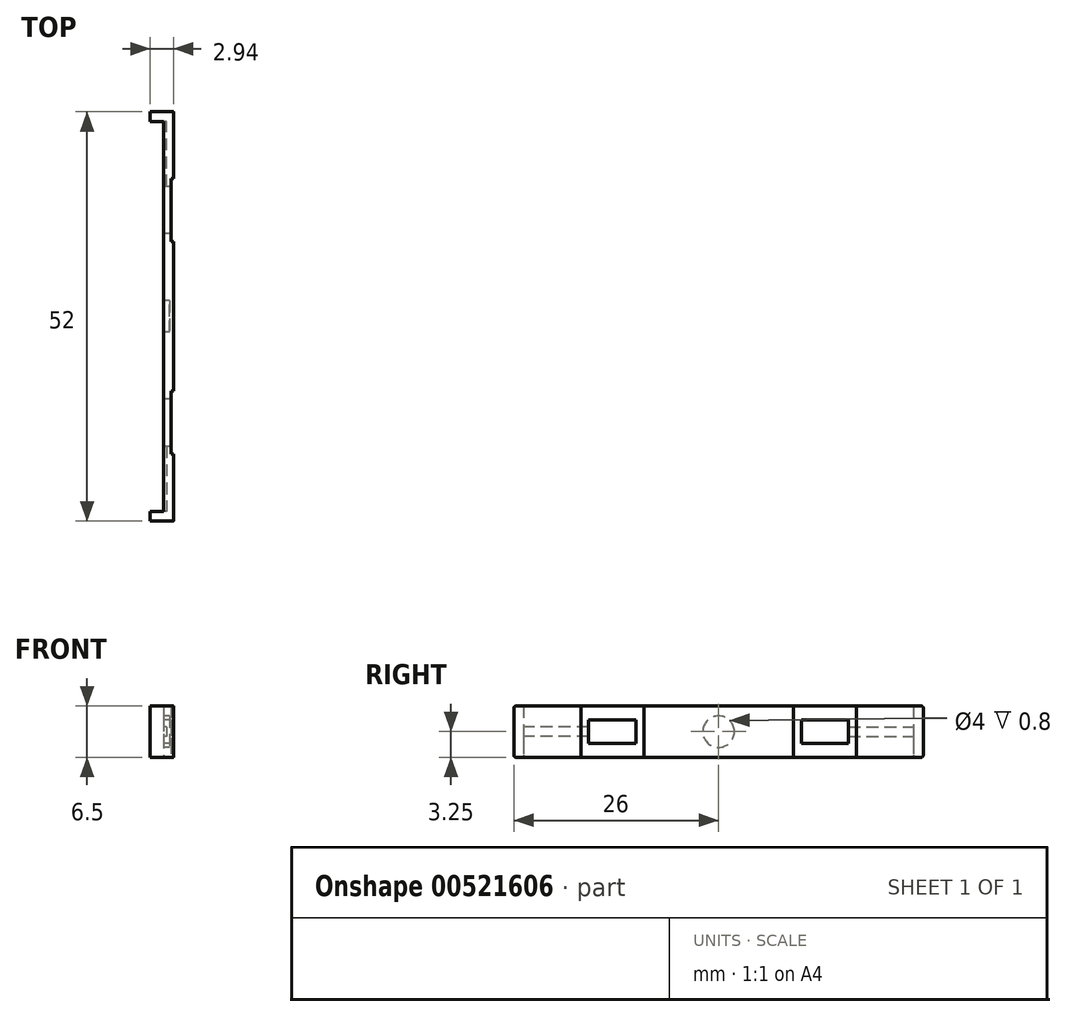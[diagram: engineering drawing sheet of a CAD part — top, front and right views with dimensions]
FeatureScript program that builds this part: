
annotation { "Feature Type Name" : "Feature", "Feature Type Description" : "" }
export const myFeature = defineFeature(function(context is Context, id is Id, definition is map)
    precondition{}
    {
        {
            var Q0;
            Q0=qCreatedBy(makeId("Right.planeOp"),FACE);
            var sketch = newSketch(context, id + "F0", { "sketchPlane" : qUnion([Q0])});
            skLineSegment(sketch, "E0.bottom", {"start": v(26, 3.25) * mm, "end": v(-26, 3.25) * mm});
            skLineSegment(sketch, "E0.top", {"start": v(26, -3.25) * mm, "end": v(-26, -3.25) * mm});
            skLineSegment(sketch, "E0.left", {"start": v(26, 3.25) * mm, "end": v(26, -3.25) * mm});
            skLineSegment(sketch, "E0.right", {"start": v(-26, 3.25) * mm, "end": v(-26, -3.25) * mm});
            skPoint(sketch, "E0.middle", {"position": v(0, 0) * mm});
            skSolve(sketch);
        }
        {
            var Q0;
            Q0=makeQuery(id+"F0.imprint","IMPRINT",FACE,{"disambiguationData":[TD([[makeQuery(id+"F0.imprint","IMPRINT",EDGE,{"derivedFrom":sQuery(id+"F0.wireOp",EDGE,"E0.bottom")}),1.0]])]});
            extrude(context, id + "F1", {"entities" : qUnion([Q0]), "endBound" : BoundingType.SYMMETRIC, "depth" : 1.25 * mm, "offsetDistance" : 25 * mm});
        }
        {
            var Q0;
            Q0=makeQuery(id+"F1.opExtrude","CAP_FACE",FACE,{"disambiguationData":[OSD([sQuery(id+"F0.wireOp",EDGE,"E0.bottom"),sQuery(id+"F0.wireOp",EDGE,"E0.top"),sQuery(id+"F0.wireOp",EDGE,"E0.left"),sQuery(id+"F0.wireOp",EDGE,"E0.right")])],"isStart":true});
            var sketch = newSketch(context, id + "F2", { "sketchPlane" : qUnion([Q0])});
            skLineSegment(sketch, "E1.bottom", {"start": v(-26, 3.25) * mm, "end": v(-24.75, 3.25) * mm});
            skLineSegment(sketch, "E1.top", {"start": v(-26, -3.25) * mm, "end": v(-24.75, -3.25) * mm});
            skLineSegment(sketch, "E1.left", {"start": v(-26, 3.25) * mm, "end": v(-26, -3.25) * mm});
            skLineSegment(sketch, "E1.right", {"start": v(-24.75, 3.25) * mm, "end": v(-24.75, -3.25) * mm});
            skLineSegment(sketch, "E2.bottom", {"start": v(24.75, 3.25) * mm, "end": v(26, 3.25) * mm});
            skLineSegment(sketch, "E2.top", {"start": v(24.75, -3.25) * mm, "end": v(26, -3.25) * mm});
            skLineSegment(sketch, "E2.left", {"start": v(24.75, 3.25) * mm, "end": v(24.75, -3.25) * mm});
            skLineSegment(sketch, "E2.right", {"start": v(26, 3.25) * mm, "end": v(26, -3.25) * mm});
            skSolve(sketch);
        }
        {
            var Q0;
            Q0=qSketchRegion(id+"F2",true);
            extrude(context, id + "F3", {"entities" : qUnion([Q0]), "operationType" : NewBodyOperationType.ADD, "depth" : 1.7 * mm, "offsetDistance" : 25 * mm});
        }
        {
            var Q0;
            Q0=makeQuery(id+"F3.boolean.opBoolean","MERGE",EDGE,{"derivedFrom":[makeQuery(id+"F1.opExtrude","SWEPT_EDGE",EDGE,{"disambiguationData":[OSD([sQuery(id+"F0.wireOp",EDGE,"E0.bottom"),sQuery(id+"F0.wireOp",EDGE,"E0.right")])]}),makeQuery(id+"F3.opExtrude","SWEPT_EDGE",EDGE,{"disambiguationData":[OSD([sQuery(id+"F2.wireOp",EDGE,"E2.bottom"),sQuery(id+"F2.wireOp",EDGE,"E2.right")])]})]});
            var Q1;
            Q1=makeQuery(id+"F3.boolean.opBoolean","MERGE",EDGE,{"derivedFrom":[makeQuery(id+"F1.opExtrude","SWEPT_EDGE",EDGE,{"disambiguationData":[OSD([sQuery(id+"F0.wireOp",EDGE,"E0.top"),sQuery(id+"F0.wireOp",EDGE,"E0.right")])]}),makeQuery(id+"F3.opExtrude","SWEPT_EDGE",EDGE,{"disambiguationData":[OSD([sQuery(id+"F2.wireOp",EDGE,"E2.top"),sQuery(id+"F2.wireOp",EDGE,"E2.right")])]})]});
            var Q2;
            Q2=makeQuery(id+"F3.boolean.opBoolean","MERGE",EDGE,{"derivedFrom":[makeQuery(id+"F1.opExtrude","SWEPT_EDGE",EDGE,{"disambiguationData":[OSD([sQuery(id+"F0.wireOp",EDGE,"E0.bottom"),sQuery(id+"F0.wireOp",EDGE,"E0.left")])]}),makeQuery(id+"F3.opExtrude","SWEPT_EDGE",EDGE,{"disambiguationData":[OSD([sQuery(id+"F2.wireOp",EDGE,"E1.bottom"),sQuery(id+"F2.wireOp",EDGE,"E1.left")])]})]});
            var Q3;
            Q3=makeQuery(id+"F3.boolean.opBoolean","MERGE",EDGE,{"derivedFrom":[makeQuery(id+"F1.opExtrude","SWEPT_EDGE",EDGE,{"disambiguationData":[OSD([sQuery(id+"F0.wireOp",EDGE,"E0.top"),sQuery(id+"F0.wireOp",EDGE,"E0.left")])]}),makeQuery(id+"F3.opExtrude","SWEPT_EDGE",EDGE,{"disambiguationData":[OSD([sQuery(id+"F2.wireOp",EDGE,"E1.top"),sQuery(id+"F2.wireOp",EDGE,"E1.left")])]})]});
            fillet(context, id + "F4", {"entities" : qUnion([Q0, Q1, Q2, Q3]), "radius" : .25 * mm, "tangentPropagation" : true, "allowEdgeOverflow" : false});
        }
        {
            var Q0;
            Q0=makeQuery(id+"F1.opExtrude","CAP_FACE",FACE,{"disambiguationData":[OSD([sQuery(id+"F0.wireOp",EDGE,"E0.bottom"),sQuery(id+"F0.wireOp",EDGE,"E0.top"),sQuery(id+"F0.wireOp",EDGE,"E0.left"),sQuery(id+"F0.wireOp",EDGE,"E0.right")])],"isStart":true});
            var sketch = newSketch(context, id + "F5", { "sketchPlane" : qUnion([Q0])});
            skCircle(sketch, "E3", {"center": v(0, 0) * mm, "radius": 2 * mm});
            skSolve(sketch);
        }
        {
            var Q0;
            Q0=makeQuery(id+"F5.imprint","IMPRINT",FACE,{"disambiguationData":[TD([[makeQuery(id+"F5.imprint","IMPRINT",EDGE,{"derivedFrom":sQuery(id+"F5.wireOp",EDGE,"E3")}),1.0]])]});
            extrude(context, id + "F6", {"entities" : qUnion([Q0]), "operationType" : NewBodyOperationType.REMOVE, "oppositeDirection" : true, "depth" : .8 * mm, "offsetDistance" : 25 * mm});
        }
        {
            var Q0;
            Q0=makeQuery(id+"F1.opExtrude","CAP_FACE",FACE,{"disambiguationData":[OSD([sQuery(id+"F0.wireOp",EDGE,"E0.bottom"),sQuery(id+"F0.wireOp",EDGE,"E0.top"),sQuery(id+"F0.wireOp",EDGE,"E0.left"),sQuery(id+"F0.wireOp",EDGE,"E0.right")])],"isStart":false});
            var sketch = newSketch(context, id + "F7", { "sketchPlane" : qUnion([Q0])});
            skLineSegment(sketch, "E4.bottom", {"start": v(-9.5, 3.25) * mm, "end": v(-17.5, 3.25) * mm});
            skLineSegment(sketch, "E4.top", {"start": v(-9.5, -3.25) * mm, "end": v(-17.5, -3.25) * mm});
            skLineSegment(sketch, "E4.left", {"start": v(-9.5, 3.25) * mm, "end": v(-9.5, -3.25) * mm});
            skLineSegment(sketch, "E4.right", {"start": v(-17.5, 3.25) * mm, "end": v(-17.5, -3.25) * mm});
            skPoint(sketch, "E4.middle", {"position": v(-13.5, 0) * mm});
            skLineSegment(sketch, "E5.bottom", {"start": v(9.5, 3.25) * mm, "end": v(17.5, 3.25) * mm});
            skLineSegment(sketch, "E5.top", {"start": v(9.5, -3.25) * mm, "end": v(17.5, -3.25) * mm});
            skLineSegment(sketch, "E5.left", {"start": v(9.5, 3.25) * mm, "end": v(9.5, -3.25) * mm});
            skLineSegment(sketch, "E5.right", {"start": v(17.5, 3.25) * mm, "end": v(17.5, -3.25) * mm});
            skPoint(sketch, "E5.middle", {"position": v(13.5, 0) * mm});
            skSolve(sketch);
        }
        {
            var Q0;
            Q0 = qSketchRegion(id + "F7", true);
            extrude(context, id + "F8", {"entities" : qUnion([Q0]), "operationType" : NewBodyOperationType.REMOVE, "oppositeDirection" : true, "depth" : .3 * mm, "offsetDistance" : 25 * mm});
        }
        {
            var Q0;
            Q0=makeQuery(id+"F1.opExtrude","CAP_FACE",FACE,{"disambiguationData":[OSD([sQuery(id+"F0.wireOp",EDGE,"E0.bottom"),sQuery(id+"F0.wireOp",EDGE,"E0.top"),sQuery(id+"F0.wireOp",EDGE,"E0.left"),sQuery(id+"F0.wireOp",EDGE,"E0.right")])],"isStart":true});
            var sketch = newSketch(context, id + "F9", { "sketchPlane" : qUnion([Q0])});
            skLineSegment(sketch, "E6.bottom", {"start": v(16.5, -1.5) * mm, "end": v(10.5, -1.5) * mm});
            skLineSegment(sketch, "E6.top", {"start": v(16.5, 1.5) * mm, "end": v(10.5, 1.5) * mm});
            skLineSegment(sketch, "E6.left", {"start": v(16.5, -1.5) * mm, "end": v(16.5, 1.5) * mm});
            skLineSegment(sketch, "E6.right", {"start": v(10.5, -1.5) * mm, "end": v(10.5, 1.5) * mm});
            skPoint(sketch, "E6.middle", {"position": v(13.5, 0) * mm});
            skLineSegment(sketch, "E7.bottom", {"start": v(-16.5, 1.5) * mm, "end": v(-10.5, 1.5) * mm});
            skLineSegment(sketch, "E7.top", {"start": v(-16.5, -1.5) * mm, "end": v(-10.5, -1.5) * mm});
            skLineSegment(sketch, "E7.left", {"start": v(-16.5, 1.5) * mm, "end": v(-16.5, -1.5) * mm});
            skLineSegment(sketch, "E7.right", {"start": v(-10.5, 1.5) * mm, "end": v(-10.5, -1.5) * mm});
            skPoint(sketch, "E7.middle", {"position": v(-13.5, 0) * mm});
            skSolve(sketch);
        }
        {
            var Q0;
            Q0 = qSketchRegion(id + "F9", true);
            extrude(context, id + "F10", {"entities" : qUnion([Q0]), "operationType" : NewBodyOperationType.REMOVE, "endBound" : BoundingType.UP_TO_NEXT, "oppositeDirection" : true, "depth" : 25 * mm, "offsetDistance" : 25 * mm});
        }
        {
            var Q0;
            Q0=makeQuery(id+"F1.opExtrude","CAP_FACE",FACE,{"disambiguationData":[OSD([sQuery(id+"F0.wireOp",EDGE,"E0.bottom"),sQuery(id+"F0.wireOp",EDGE,"E0.top"),sQuery(id+"F0.wireOp",EDGE,"E0.left"),sQuery(id+"F0.wireOp",EDGE,"E0.right")])],"isStart":true});
            var sketch = newSketch(context, id + "F11", { "sketchPlane" : qUnion([Q0])});
            skLineSegment(sketch, "E8.bottom", {"start": v(-16.5, 0.63) * mm, "end": v(-24.75, 0.63) * mm});
            skLineSegment(sketch, "E8.top", {"start": v(-16.5, -0.62) * mm, "end": v(-24.75, -0.62) * mm});
            skLineSegment(sketch, "E8.left", {"start": v(-16.5, 0.63) * mm, "end": v(-16.5, -0.62) * mm});
            skLineSegment(sketch, "E8.right", {"start": v(-24.75, 0.63) * mm, "end": v(-24.75, -0.62) * mm});
            skPoint(sketch, "E8.middle", {"position": v(-20.62, 0) * mm});
            skPoint(sketch, "E8.middle.positionSnap0", {"position": v(-16.5, 0) * mm});
            skPoint(sketch, "E8.centerSnap0", {"position": v(-16.5, 0) * mm});
            skLineSegment(sketch, "E9.bottom", {"start": v(16.5, 0.62) * mm, "end": v(24.75, 0.62) * mm});
            skLineSegment(sketch, "E9.top", {"start": v(16.5, -0.63) * mm, "end": v(24.75, -0.63) * mm});
            skLineSegment(sketch, "E9.left", {"start": v(16.5, 0.62) * mm, "end": v(16.5, -0.63) * mm});
            skLineSegment(sketch, "E9.right", {"start": v(24.75, 0.62) * mm, "end": v(24.75, -0.63) * mm});
            skPoint(sketch, "E9.middle", {"position": v(20.62, 0) * mm});
            skPoint(sketch, "E9.middle.positionSnap0", {"position": v(16.5, 0) * mm});
            skPoint(sketch, "E9.centerSnap0", {"position": v(16.5, 0) * mm});
            skSolve(sketch);
        }
        {
            var Q0;
            Q0 = qSketchRegion(id + "F11", true);
            extrude(context, id + "F12", {"entities" : qUnion([Q0]), "operationType" : NewBodyOperationType.REMOVE, "oppositeDirection" : true, "depth" : .4 * mm, "offsetDistance" : 25 * mm});
        }
    });
